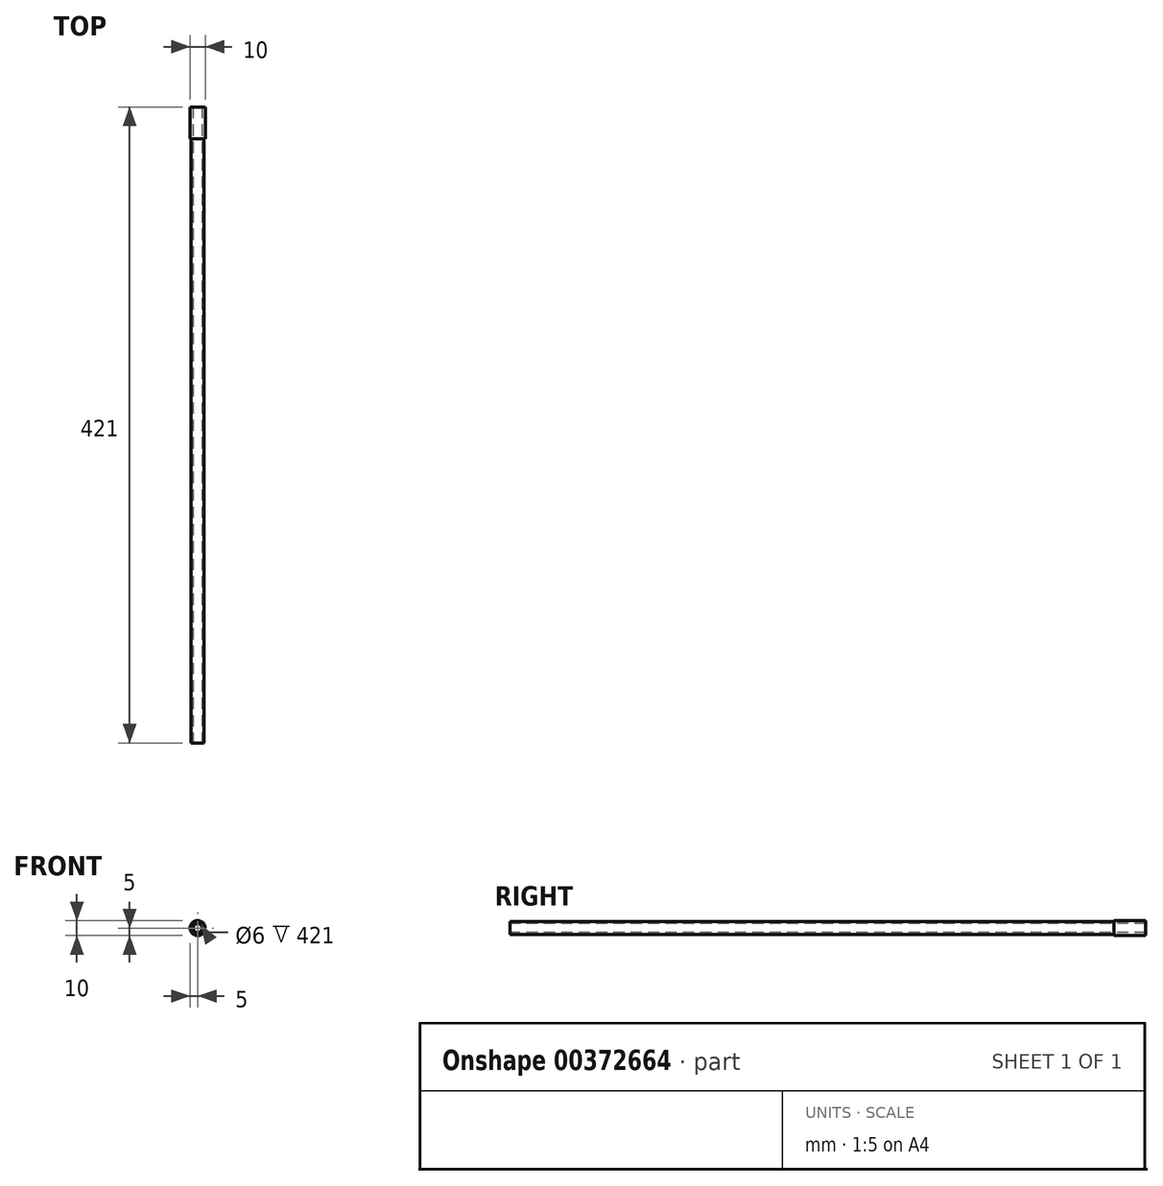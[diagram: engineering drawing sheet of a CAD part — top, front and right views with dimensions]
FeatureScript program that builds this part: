
annotation { "Feature Type Name" : "Feature", "Feature Type Description" : "" }
export const myFeature = defineFeature(function(context is Context, id is Id, definition is map)
    precondition{}
    {
        {
            var Q0;
            Q0=qCreatedBy(makeId("Front.planeOp"),FACE);
            var sketch = newSketch(context, id + "F0", { "sketchPlane" : qUnion([Q0])});
            skCircle(sketch, "E0", {"center": v(0, 0) * mm, "radius": 4.25 * mm});
            skCircle(sketch, "E1", {"center": v(0, 0) * mm, "radius": 3 * mm});
            skCircle(sketch, "E2", {"center": v(0, 0) * mm, "radius": 5 * mm});
            skSolve(sketch);
        }
        {
            var Q0;
            Q0=makeQuery(id+"F0.imprint","IMPRINT",FACE,{"disambiguationData":[TD([[makeQuery(id+"F0.imprint","IMPRINT",EDGE,{"derivedFrom":sQuery(id+"F0.wireOp",EDGE,"E0")}),1.0]])]});
            extrude(context, id + "F1", {"entities" : qUnion([Q0]), "oppositeDirection" : true, "depth" : 21 * mm, "offsetDistance" : 25 * mm, "hasSecondDirection" : true, "secondDirectionOppositeDirection" : false, "secondDirectionDepth" : 400 * mm});
        }
        {
            var Q0;
            Q0=makeQuery(id+"F0.imprint","IMPRINT",FACE,{"disambiguationData":[TD([[makeQuery(id+"F0.imprint","IMPRINT",EDGE,{"derivedFrom":sQuery(id+"F0.wireOp",EDGE,"E0")}),-1.0]])]});
            extrude(context, id + "F2", {"entities" : qUnion([Q0]), "operationType" : NewBodyOperationType.ADD, "oppositeDirection" : true, "depth" : 21 * mm, "offsetDistance" : 25 * mm});
        }
    });
